# Revit family: VL2xGP150xWSxxB
name_source: partatom
category: Leuchten
units: mm (PartAtom-declared; Revit-internal decimal feet)

## family parameters
Basisbauteil = Fläche
Beim Laden mit Abzugskörper schneiden = Nein
Bemaßung runder Anschluss = Durchmesser verwenden
Gemeinsam genutzt = Nein
Lichtquelle = Ja
OmniClass-Nummer = 23.80.70.11
OmniClass-Titel = Luminaries for Internal Lighting
Raumberechnungspunkt = Nein
Teiletyp = Normal

## types (10) — shared parameters
Baugruppenkennzeichen = D5020200
Datei für fotometrisches Netz = Master_VL1GP1486-5RFWS840B0900.IES
Emissionsform beim Rendern sichtbar = Nein
Farbfilter = 16777215
Farbtemperaturverschiebung bei Dämpfen der Lampe = <Keine Auswahl>
Hersteller = RIDI Leuchten GmbH
Lampe = LED
Neigungswinkel = 90.00°
URL = www.ridi.de
Von Breite des Rechtecks ausssenden = 1479 mm  [stored 4.85236 ft]
Von Länge des Rechtecks aussenden = 61 mm  [stored 0.200131 ft]
brand = RIDI
conformity mark = CE
electrical safety class = 1
height = 64 mm  [stored 0.209974 ft]
ingress protection (IP) code = IP20
length = 1500 mm  [stored 4.92126 ft]
nominal frequency = 50-60Hz
nominal voltage = 230
voltage type (AC, DC, UC) = AC
weight = 1,7kg
width = 67 mm
zero-valued in all types: Vorgabe-Ansicht

## per-type parameters (varying)
| type | Modell | Scheinlast | rated input power |
| VL2E-GP150-5FLWS840B1000 | 2550015 | 63 VA | 63 |
| VL2S-GP150-5FLWS840B0900 | 2550023 | 50 VA | 50 |
| VL2S-GP150-5FLWS850B1200 | 2550055 | 71 VA | 71 |
| VL2S-GP150-5FLWS865B1200 | 2550056 | 71 VA | 71 |
| VL2P-GP150-5FLWS840B1000 | 2550077 | 59 VA | 59 |
| VL2E-GP150-7DAWS840B1000 | 2560015 | 65 VA | 65 |
| VL2S-GP150-7DAWS840B1200 | 2560050 | 73 VA | 73 |
| VL2S-GP150-7DAWS865B1200 | 2560056 | 72 VA | 72 |
| VL2S-GP150-7DAWS840B0500 | 2560058 | 30 VA | 30 |
| VL2S-GP150-7DAWS840B0900 | 2560101 | 51 VA | 51 |

note: column(s) folded — value = type name in every type: product name

note: [stored X ft] marks values corroborated as IEEE doubles in the binary element streams (Revit-internal decimal feet)
